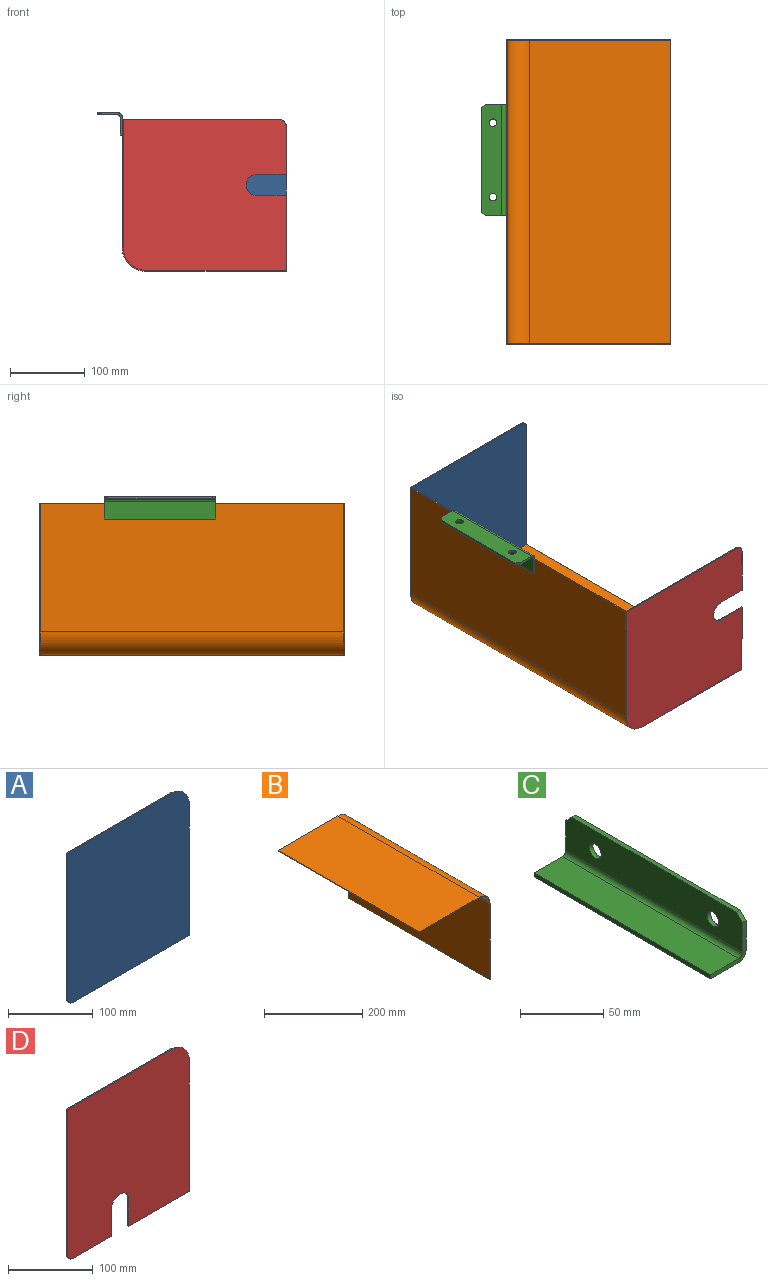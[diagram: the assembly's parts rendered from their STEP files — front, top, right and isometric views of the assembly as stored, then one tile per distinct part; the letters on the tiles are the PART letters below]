
ASSEMBLY  parts=4 mates=10
PART A: 8 faces, bbox 204x1.5x220 mm
  f0: plane 172.5x1.5mm, normal (0,0,1), area 258.8mm2, adj f1,f4,f5,f6
  f1: plane 210x1.5mm, normal (-1,0,0), area 315mm2, adj f0,f5,f6,f7
  f2: plane 194x1.5mm, normal (0,0,-1), area 291mm2, adj f3,f5,f6,f7
  f3: plane 188.5x1.5mm, normal (1,0,0), area 282.7mm2, adj f2,f4,f5,f6
  f4: cylinder r=31.5mm len=31.5mm, axis (0,1,0), area 74.2mm2, adj f0,f3,f5,f6
  f5: plane 220x204mm, normal (0,-1,0), area 44645.6mm2, adj f0,f1,f2,f3,f4,f7
  f6: plane 220x204mm, normal (0,1,0), area 44645.6mm2, adj f0,f1,f2,f3,f4,f7
  f7: cylinder r=10mm len=10mm, axis (0,1,0), area 23.6mm2, adj f1,f2,f5,f6
PART B: 10 faces, bbox 204x407x220 mm
  f0: plane 407x1.5mm, normal (0,0,-1), area 610.5mm2, adj f1,f7,f8,f9
  f1: plane 407x188.5mm, normal (1,0,0), area 76719.5mm2, adj f0,f2,f8,f9
  f2: cylinder r=31.5mm len=407mm, axis (0,1,0), area 20138.4mm2, adj f1,f3,f8,f9
  f3: plane 407x172.5mm, normal (0,0,1), area 70207.5mm2, adj f2,f4,f8,f9
  f4: plane 407x1.5mm, normal (-1,0,0), area 610.5mm2, adj f3,f5,f8,f9
  f5: plane 407x172.5mm, normal (0,0,-1), area 70207.5mm2, adj f4,f6,f8,f9
  f6: cylinder r=30mm len=407mm, axis (0,1,0), area 19179.4mm2, adj f5,f7,f8,f9
  f7: plane 407x188.5mm, normal (-1,0,0), area 76719.5mm2, adj f0,f6,f8,f9
  f8: plane 220x204mm, normal (0,-1,0), area 614mm2, adj f0,f1,f2,f3,f4,f5,f6,f7
  f9: plane 220x204mm, normal (0,1,0), area 614mm2, adj f0,f1,f2,f3,f4,f5,f6,f7
PART C: 14 faces, bbox 30x150x33 mm
  f0: plane 150x27mm, normal (-1,0,0), area 3867.9mm2, adj f1,f7,f8,f9,f10,f11,f12,f13
  f1: cylinder r=3mm len=150mm, axis (0,1,0), area 706.9mm2, adj f0,f2,f8,f9
  f2: plane 150x24mm, normal (0,0,1), area 3600mm2, adj f1,f3,f8,f9
  f3: plane 150x3mm, normal (-1,0,0), area 450mm2, adj f2,f4,f8,f9
  f4: plane 150x24mm, normal (0,0,-1), area 3600mm2, adj f3,f5,f8,f9
  f5: cylinder r=6mm len=150mm, axis (0,1,0), area 1413.7mm2, adj f4,f6,f8,f9
  f6: plane 150x27mm, normal (1,0,0), area 3867.9mm2, adj f5,f7,f8,f9,f10,f11,f12,f13
  f7: plane 140x3mm, normal (0,0,1), area 420mm2, adj f0,f6,f10,f11
  f8: plane 30x28mm, normal (0,-1,0), area 159.2mm2, adj f0,f1,f2,f3,f4,f5,f6,f11
  f9: plane 30x28mm, normal (0,1,0), area 159.2mm2, adj f0,f1,f2,f3,f4,f5,f6,f10
  f10: plane 5x5mm, normal (0,0.71,0.71), area 21.2mm2, adj f0,f6,f7,f9
  f11: plane 5x5mm, normal (0,-0.71,0.71), area 21.2mm2, adj f0,f6,f7,f8
  f12: cylinder r=5mm len=10mm, axis (-1,0,0), area 94.2mm2, adj f0,f6
  f13: cylinder r=5mm len=10mm, axis (-1,0,0), area 94.2mm2, adj f0,f6
PART D: 12 faces, bbox 204x1.5x220 mm
  f0: plane 102x1.5mm, normal (0,0,-1), area 153mm2, adj f4,f6,f7,f9
  f1: plane 172.5x1.5mm, normal (0,0,1), area 258.8mm2, adj f2,f5,f6,f7
  f2: plane 210x1.5mm, normal (-1,0,0), area 315mm2, adj f1,f6,f7,f8
  f3: plane 64x1.5mm, normal (0,0,-1), area 96mm2, adj f6,f7,f8,f11
  f4: plane 188.5x1.5mm, normal (1,0,0), area 282.7mm2, adj f0,f5,f6,f7
  f5: cylinder r=31.5mm len=31.5mm, axis (0,1,0), area 74.2mm2, adj f1,f4,f6,f7
  f6: plane 220x204mm, normal (0,-1,0), area 43217.7mm2, adj f0,f1,f2,f3,f4,f5,f8,f9
  f7: plane 220x204mm, normal (0,1,0), area 43217.7mm2, adj f0,f1,f2,f3,f4,f5,f8,f9
  f8: cylinder r=10mm len=10mm, axis (0,1,0), area 23.6mm2, adj f2,f3,f6,f7
  f9: plane 40x1.5mm, normal (-1,0,0), area 60mm2, adj f0,f6,f7,f10
  f10: cylinder r=14mm len=28mm, axis (0,-1,0), area 66mm2, adj f6,f7,f9,f11
  f11: plane 40x1.5mm, normal (1,0,0), area 60mm2, adj f3,f6,f7,f10
PLACE A rot(axis=(-0.71,0,0.71),180deg) t=(94.25,204.25,-1.5)mm
PLACE B rot(axis=(-0.71,0,0.71),180deg) t=(94.25,0,-1.5)mm
PLACE C rot(axis=(0,-1,0),90deg) t=(-125.75,42.84,211.38)mm
PLACE D rot(axis=(-0.71,0,0.71),180deg) t=(94.25,-204.25,-1.5)mm
MATE parallel A.f0 <-> B.f3  axis (-1,0,0) through (-125.75,204.25,116.25)mm
MATE planar B.f3 <-> C.f4  axis (-1,0,0) through (-125.75,0,116.25)mm
MATE parallel C.f8 <-> D.f7  axis (0,-1,0) through (-142.75,-32.16,211.38)mm
MATE ball B.f2 <-> A.f4  axis (0,1,0) through (-94.25,203.5,30)mm
MATE parallel D.f1 <-> B.f3  axis (-1,0,0) through (-125.75,-204.25,116.25)mm
MATE parallel B.f3 <-> C.f4  axis (-1,0,0) through (-125.75,0,116.25)mm
MATE parallel B.f8 <-> A.f6  axis (0,1,0) through (-66.11,203.5,49.88)mm
MATE parallel D.f4 <-> B.f1  axis (0,0,-1) through (0,-204.25,-1.5)mm
MATE parallel B.f9 <-> D.f6  axis (0,-1,0) through (-66.11,-203.5,49.88)mm
MATE ball D.f5 <-> B.f2  axis (0,1,0) through (-94.25,-203.5,30)mm
